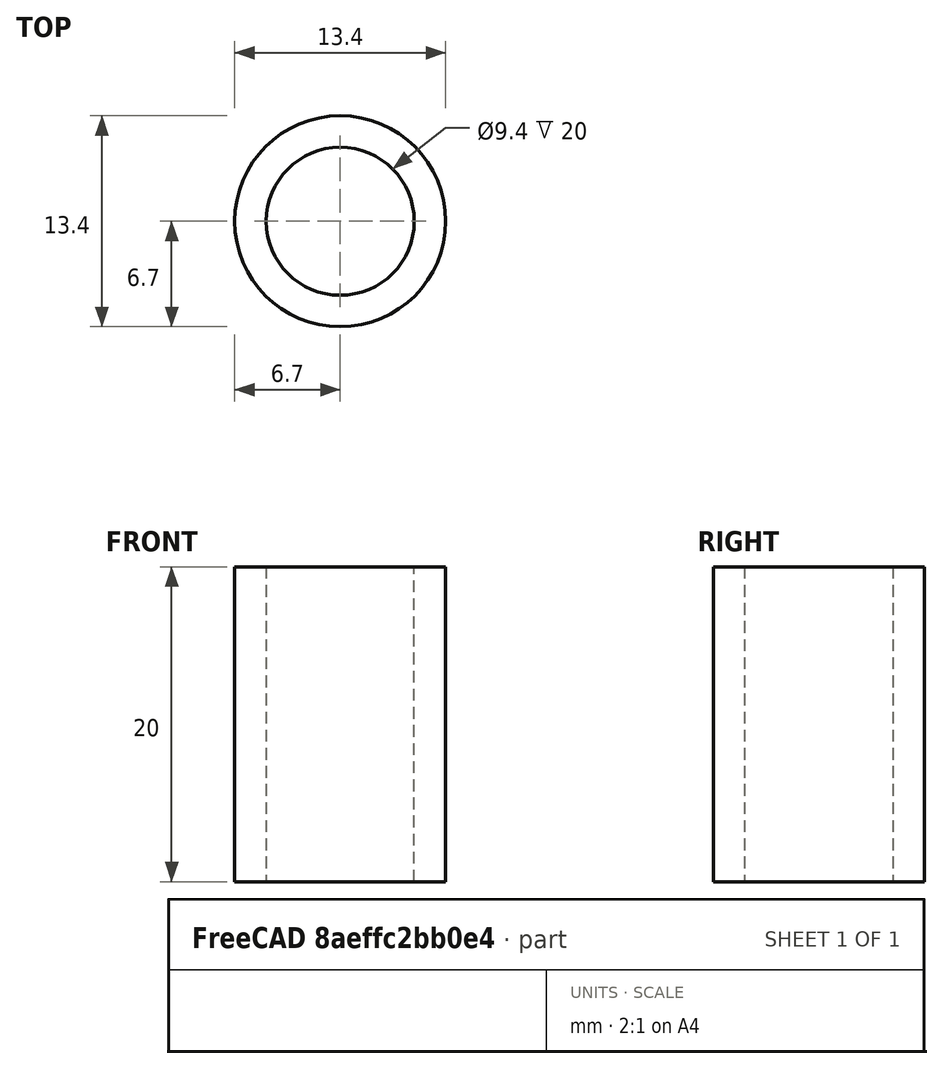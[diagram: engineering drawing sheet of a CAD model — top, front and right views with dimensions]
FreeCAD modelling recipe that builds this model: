
FCSTD DOCUMENT  (FreeCAD 0.18R16110 (Git))
Label: testv3
License: All rights reserved
LicenseURL: http://en.wikipedia.org/wiki/All_rights_reserved
objects: Sketcher::SketchObject×1, PartDesign::Pad×1, PartDesign::Body×1
note: 4 computed .brp shape members not serialized (recipe doc carries the construction recipe); baked Part::Feature solids carry a one-line shape summary decoded from their .brp

FEATURE [Sketcher::SketchObject] Sketch
  MapMode = 5
  Support = -> [XY_Plane]
  sketch-geometry (2):
    g0: Circle CenterX=0 CenterY=0 CenterZ=0 NormalX=0 NormalY=0 NormalZ=1 AngleXU=0 Radius=6.7
    g1: Circle CenterX=0 CenterY=0 CenterZ=0 NormalX=0 NormalY=0 NormalZ=1 AngleXU=0 Radius=4.7
  constraints (4):
    c: Coincident(g0,g-1)
    c: Coincident(g1,g0)
    c: Radius(g1) = 4.7
    c: Radius(g0) = 6.7
FEATURE [PartDesign::Pad] Pad
  Length = 20
  Length2 = 100
  Profile = -> Sketch
  Type = 0
FEATURE [PartDesign::Body] Body
  Group = -> [Sketch,Pad]
  Origin = -> Origin
  Tip = -> Pad
